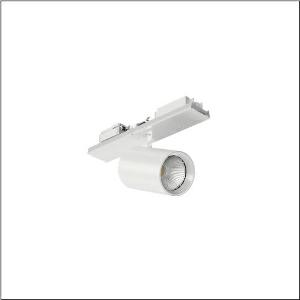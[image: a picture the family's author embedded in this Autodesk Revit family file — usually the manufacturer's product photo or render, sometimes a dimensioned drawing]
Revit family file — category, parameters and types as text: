
# Revit family: licross_r__spot_31_51sl127a43b_2c6e
name_source: partatom
category: Lighting Fixtures
units: mm (PartAtom-declared; Revit-internal decimal feet)

## family parameters
Cut with Voids When Loaded = No
Host = Face
Light Source = No
Part Type = Normal
Room Calculation Point = No
Round Connector Dimension = Use Diameter
Shared = No

## types (1)
- --- (1 x LED, 3650 lm, 28 W, 4000K)
    Apparent Load = 28 VA
    CIE Flux Codes = 93 97 99 100 100
    Color Rendering = 90
    Color Temperature = 4000K
    Default Elevation = 1800 mm
    Description = Licross® Spot 31, directional spotlight, light control with lens, of plastic, LED rated luminous flux: 3.650lm, light colour: 940, with plug, 3-pole, with phase selection, mains connection: 220..240V, AC, 50/60Hz, of aluminium, traffic white (RAL 9016), length: 140mm, diameter: 90mm, protection rating (complete): IP20, insulation class (complete): insulation class I (protective earthing), certification: CE, packaging unit: 1 piece
    Height = 175 mm
    Lamp = 1 x LED
    Lamp Light Flux = 3650 lm
    Lamp Power = 28 W
    Lamp count = 1
    Length = 90 mm
    Luminous efficacy = 130 lm/W
    Manufacturer = Siteco
    ModVariant = No
    Model = 51SL127A43B
    Mounting Place = Ceiling
    Mounting Type = Pendant
    Number of Poles = 1
    OnlyDefault = Yes
    Power Factor = 1
    Product Name = Licross® Spot 31
    Product group = directional spotlight
    ProductGroupID = 905
    Protection Class = Protection class I
    Protection Degree = IP 20
    RLX_Detail_Level = 1
    RLX_Emergency_Light_Flux = 0 lm
    RLX_Emergency_Type = 0
    RLX_Emergency_Type_DB = No
    RlxData = <blob elided: 14897 chars, md5=a99ce114>
    Socket = socket
    Standby Power = 0 W
    System Light Flux = 3650 lm
    System Power = 28 W
    Type Comments = factory setting: luminous flux: 100 % | (ON | ON | ON) | 700 mA
    Type Image = l_1245720.jpg
    URL = http://relux.com
    VarID = @adj_082163
    Voltage = 0 V
    Weight = 0.00 kg
    Width = 0 mm  [stored 0 ft]

note: [stored X ft] marks values corroborated as IEEE doubles in the binary element streams (Revit-internal decimal feet)

## geometry (parser evidence)
native form markers: Sweep x12
no freeform markers — native parametric forms only
